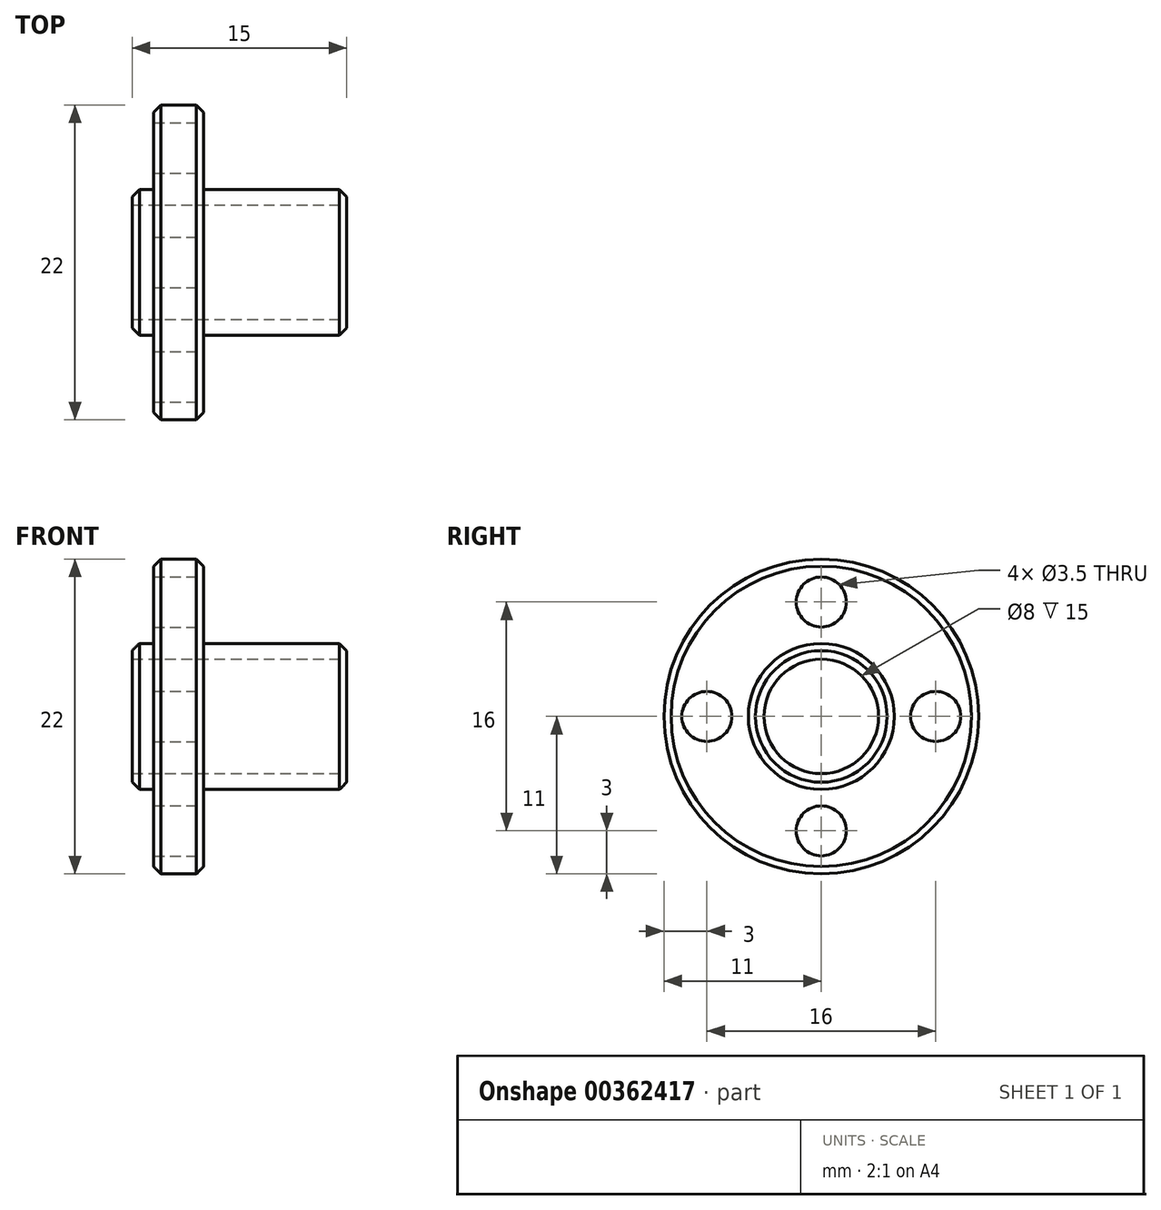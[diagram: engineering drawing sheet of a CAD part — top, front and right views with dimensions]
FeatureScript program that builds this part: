
annotation { "Feature Type Name" : "Feature", "Feature Type Description" : "" }
export const myFeature = defineFeature(function(context is Context, id is Id, definition is map)
    precondition{}
    {
        {
            var Q0;
            Q0=qCreatedBy(makeId("Right.planeOp"),FACE);
            var sketch = newSketch(context, id + "F0", { "sketchPlane" : qUnion([Q0])});
            skCircle(sketch, "E0", {"center": v(0, 0) * mm, "radius": 11 * mm});
            skSolve(sketch);
        }
        {
            var Q0;
            Q0=qSketchRegion(id+"F0",true);
            extrude(context, id + "F1", {"entities" : qUnion([Q0]), "depth" : 3.5 * mm});
        }
        {
            var Q0;
            Q0=makeQuery(id+"F1.opExtrude","CAP_FACE",FACE,{"disambiguationData":[OSD([sQuery(id+"F0.wireOp",EDGE,"E0")])],"isStart":false});
            var sketch = newSketch(context, id + "F2", { "sketchPlane" : qUnion([Q0])});
            skCircle(sketch, "E1", {"center": v(0, 0) * mm, "radius": 5.1 * mm});
            skSolve(sketch);
        }
        {
            var Q0;
            Q0=qSketchRegion(id+"F2",true);
            extrude(context, id + "F3", {"entities" : qUnion([Q0]), "operationType" : NewBodyOperationType.ADD, "depth" : 10 * mm});
        }
        {
            var Q0;
            Q0=makeQuery(id+"F3.opExtrude","CAP_FACE",FACE,{"disambiguationData":[OSD([sQuery(id+"F2.wireOp",EDGE,"E1")])],"isStart":false});
            var sketch = newSketch(context, id + "F4", { "sketchPlane" : qUnion([Q0])});
            skCircle(sketch, "E2", {"center": v(0, 0) * mm, "radius": 4 * mm});
            skSolve(sketch);
        }
        {
            var Q0;
            Q0=qSketchRegion(id+"F4",true);
            extrude(context, id + "F5", {"entities" : qUnion([Q0]), "operationType" : NewBodyOperationType.REMOVE, "oppositeDirection" : true, "depth" : 25 * mm});
        }
        {
            var Q0;
            Q0=makeQuery(id+"F1.opExtrude","CAP_FACE",FACE,{"disambiguationData":[OSD([sQuery(id+"F0.wireOp",EDGE,"E0")])],"isStart":true});
            var sketch = newSketch(context, id + "F6", { "sketchPlane" : qUnion([Q0])});
            skCircle(sketch, "E3", {"center": v(0, 0) * mm, "radius": 4 * mm});
            skCircle(sketch, "E4", {"center": v(0, 0) * mm, "radius": 5.1 * mm});
            skSolve(sketch);
        }
        {
            var Q0;
            Q0=qSketchRegion(id+"F6",true);
            extrude(context, id + "F7", {"entities" : qUnion([Q0]), "operationType" : NewBodyOperationType.ADD, "depth" : 1.5 * mm});
        }
        {
            var Q0;
            Q0=makeQuery(id+"F3.opExtrude","CAP_EDGE",EDGE,{"disambiguationData":[OSD([sQuery(id+"F2.wireOp",EDGE,"E1")])],"isStart":false});
            var Q1;
            Q1=makeQuery(id+"F1.opExtrude","CAP_EDGE",EDGE,{"disambiguationData":[OSD([sQuery(id+"F0.wireOp",EDGE,"E0")])],"isStart":false});
            var Q2;
            Q2=makeQuery(id+"F1.opExtrude","CAP_EDGE",EDGE,{"disambiguationData":[OSD([sQuery(id+"F0.wireOp",EDGE,"E0")])],"isStart":true});
            var Q3;
            Q3=makeQuery(id+"F7.opExtrude","CAP_EDGE",EDGE,{"disambiguationData":[OSD([sQuery(id+"F6.wireOp",EDGE,"E4")])],"isStart":false});
            var Q4;
            Q4=makeQuery(id+"F3.opExtrude","CAP_EDGE",EDGE,{"disambiguationData":[OSD([sQuery(id+"F2.wireOp",EDGE,"E1")])],"isStart":true});
            chamfer(context, id + "F8", {"entities" : qUnion([Q0, Q1, Q2, Q3, Q4]), "width" : 0.5 * mm, "tangentPropagation" : true});
        }
        {
            var Q0;
            Q0=makeQuery(id+"F1.opExtrude","CAP_FACE",FACE,{"disambiguationData":[OSD([sQuery(id+"F0.wireOp",EDGE,"E0")])],"isStart":false});
            var sketch = newSketch(context, id + "F9", { "sketchPlane" : qUnion([Q0])});
            skCircle(sketch, "E5", {"center": v(0, 8) * mm, "radius": 1.75 * mm});
            skCircle(sketch, "E6.1.0", {"center": v(-8, 0) * mm, "radius": 1.75 * mm});
            skCircle(sketch, "E6.2.0", {"center": v(0, -8) * mm, "radius": 1.75 * mm});
            skCircle(sketch, "E6.3.0", {"center": v(8, 0) * mm, "radius": 1.75 * mm});
            skPoint(sketch, "E6.center", {"position": v(0, 0) * mm});
            skSolve(sketch);
        }
        {
            var Q0;
            Q0=makeQuery(id+"F9.imprint","IMPRINT",FACE,{"disambiguationData":[TD([[makeQuery(id+"F9.imprint","IMPRINT",EDGE,{"derivedFrom":sQuery(id+"F9.wireOp",EDGE,"E5")}),1.0]])]});
            var Q1;
            Q1=makeQuery(id+"F9.imprint","IMPRINT",FACE,{"disambiguationData":[TD([[makeQuery(id+"F9.imprint","IMPRINT",EDGE,{"derivedFrom":sQuery(id+"F9.wireOp",EDGE,"E6.1.0")}),1.0]])]});
            var Q2;
            Q2=makeQuery(id+"F9.imprint","IMPRINT",FACE,{"disambiguationData":[TD([[makeQuery(id+"F9.imprint","IMPRINT",EDGE,{"derivedFrom":sQuery(id+"F9.wireOp",EDGE,"E6.2.0")}),1.0]])]});
            var Q3;
            Q3=makeQuery(id+"F9.imprint","IMPRINT",FACE,{"disambiguationData":[TD([[makeQuery(id+"F9.imprint","IMPRINT",EDGE,{"derivedFrom":sQuery(id+"F9.wireOp",EDGE,"E6.3.0")}),1.0]])]});
            extrude(context, id + "F10", {"entities" : qUnion([Q0, Q1, Q2, Q3]), "operationType" : NewBodyOperationType.REMOVE, "endBound" : BoundingType.THROUGH_ALL, "oppositeDirection" : true, "depth" : 25 * mm});
        }
    });
